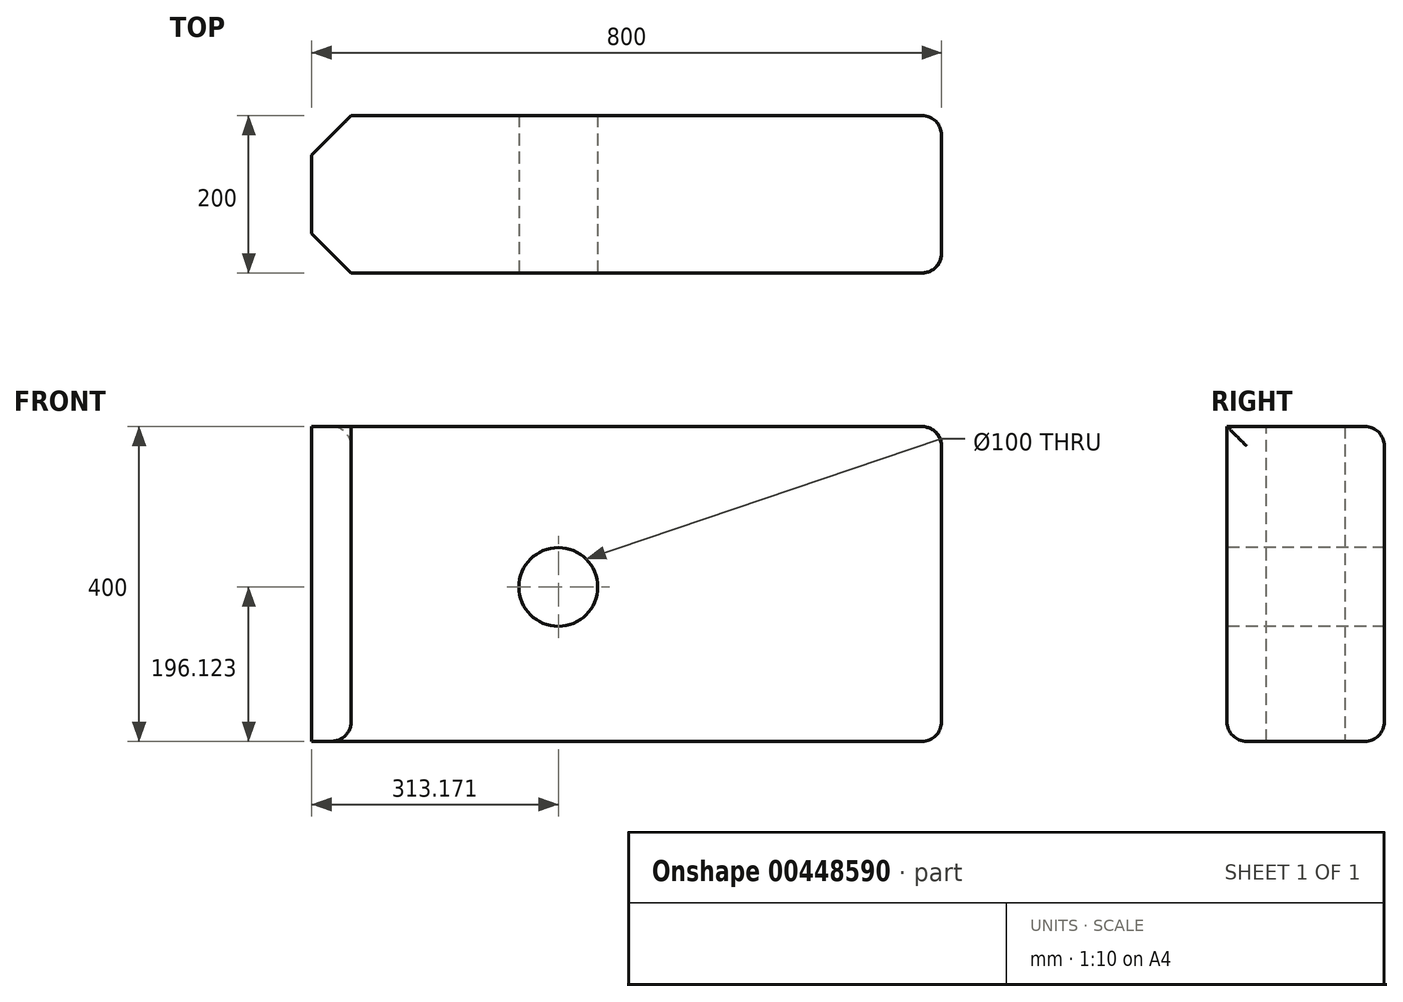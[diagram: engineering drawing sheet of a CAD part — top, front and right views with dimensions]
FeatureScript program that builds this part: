
annotation { "Feature Type Name" : "Feature", "Feature Type Description" : "" }
export const myFeature = defineFeature(function(context is Context, id is Id, definition is map)
    precondition{}
    {
        {
            var Q0;
            Q0=qCreatedBy(makeId("Front.planeOp"),FACE);
            var sketch = newSketch(context, id + "F0", { "sketchPlane" : qUnion([Q0])});
            skLineSegment(sketch, "E0.bottom", {"start": v(-400, 200) * mm, "end": v(400, 200) * mm});
            skLineSegment(sketch, "E0.top", {"start": v(-400, -200) * mm, "end": v(400, -200) * mm});
            skLineSegment(sketch, "E0.left", {"start": v(-400, 200) * mm, "end": v(-400, -200) * mm});
            skLineSegment(sketch, "E0.right", {"start": v(400, 200) * mm, "end": v(400, -200) * mm});
            skPoint(sketch, "E0.middle", {"position": v(0, 0) * mm});
            skSolve(sketch);
        }
        {
            var Q0;
            Q0=makeQuery(id+"F0.imprint","IMPRINT",FACE,{"disambiguationData":[TD([[makeQuery(id+"F0.imprint","IMPRINT",EDGE,{"derivedFrom":sQuery(id+"F0.wireOp",EDGE,"E0.bottom")}),-1.0]])]});
            extrude(context, id + "F1", {"entities" : qUnion([Q0]), "depth" : 200 * mm});
        }
        {
            var Q0;
            Q0=makeQuery(id+"F1.opExtrude","CAP_EDGE",EDGE,{"disambiguationData":[OSD([sQuery(id+"F0.wireOp",EDGE,"E0.left")])],"isStart":false});
            var Q1;
            Q1=makeQuery(id+"F1.opExtrude","CAP_EDGE",EDGE,{"disambiguationData":[OSD([sQuery(id+"F0.wireOp",EDGE,"E0.left")])],"isStart":true});
            chamfer(context, id + "F2", {"entities" : qUnion([Q0, Q1]), "width" : 50 * mm, "tangentPropagation" : true});
        }
        {
            var Q0;
            Q0=makeQuery(id+"F1.opExtrude","SWEPT_EDGE",EDGE,{"disambiguationData":[OSD([sQuery(id+"F0.wireOp",EDGE,"E0.top"),sQuery(id+"F0.wireOp",EDGE,"E0.right")])]});
            fillet(context, id + "F3", {"entities" : qUnion([Q0]), "radius" : 25 * mm, "tangentPropagation" : true, "allowEdgeOverflow" : false});
        }
        {
            var Q0;
            Q0=makeQuery(id+"F1.opExtrude","SWEPT_EDGE",EDGE,{"disambiguationData":[OSD([sQuery(id+"F0.wireOp",EDGE,"E0.bottom"),sQuery(id+"F0.wireOp",EDGE,"E0.right")])]});
            var Q1;
            Q1=makeQuery(id+"F1.opExtrude","CAP_EDGE",EDGE,{"disambiguationData":[OSD([sQuery(id+"F0.wireOp",EDGE,"E0.right")])],"isStart":false});
            fillet(context, id + "F4", {"entities" : qUnion([Q0, Q1]), "radius" : 25 * mm, "tangentPropagation" : true, "allowEdgeOverflow" : false});
        }
        {
            var Q0;
            Q0=makeQuery(id+"F1.opExtrude","CAP_EDGE",EDGE,{"disambiguationData":[OSD([sQuery(id+"F0.wireOp",EDGE,"E0.right")])],"isStart":true});
            fillet(context, id + "F5", {"entities" : qUnion([Q0]), "radius" : 25 * mm, "tangentPropagation" : true, "allowEdgeOverflow" : false});
        }
        {
            var Q0;
            Q0=makeQuery(id+"F1.opExtrude","CAP_FACE",FACE,{"disambiguationData":[OSD([sQuery(id+"F0.wireOp",EDGE,"E0.bottom"),sQuery(id+"F0.wireOp",EDGE,"E0.top"),sQuery(id+"F0.wireOp",EDGE,"E0.left"),sQuery(id+"F0.wireOp",EDGE,"E0.right")])],"isStart":false});
            var sketch = newSketch(context, id + "F6", { "sketchPlane" : qUnion([Q0])});
            skCircle(sketch, "E1", {"center": v(-86.83, -3.88) * mm, "radius": 50 * mm});
            skSolve(sketch);
        }
        {
            var Q0;
            Q0=sQuery(id+"F6.wireOp",VERTEX,"E1.center");
            var Q1;
            Q1=makeQuery(id+"F1.opExtrude","SWEPT_BODY",BODY,{"disambiguationData":[OSD([sQuery(id+"F0.wireOp",EDGE,"E0.bottom"),sQuery(id+"F0.wireOp",EDGE,"E0.top"),sQuery(id+"F0.wireOp",EDGE,"E0.left"),sQuery(id+"F0.wireOp",EDGE,"E0.right")])]});
            hole(context, id + "F7", {"style" : HoleStyle.SIMPLE, "endStyle" : HoleEndStyle.THROUGH, "holeDiameter" : 100 * mm, "isTappedThrough" : true, "tappedDepth" : 12 * mm, "tapClearance" : 3, "startFromSketch" : true, "locations" : qUnion([Q0]), "scope" : qUnion([Q1])});
        }
    });
